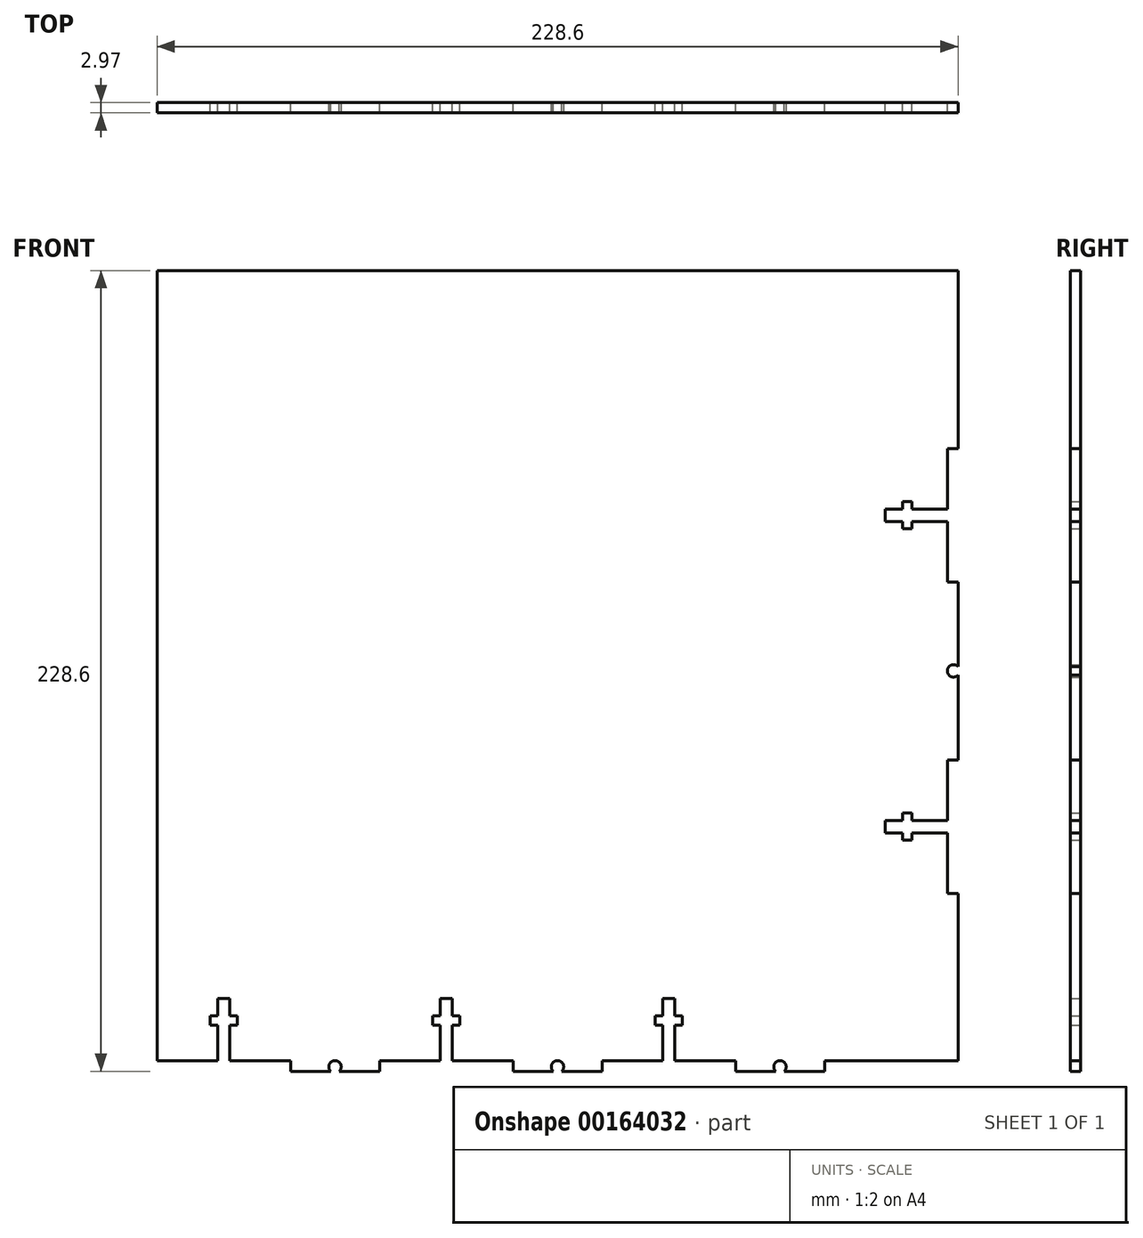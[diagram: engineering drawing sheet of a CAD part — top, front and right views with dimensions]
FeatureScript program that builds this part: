
annotation { "Feature Type Name" : "Feature", "Feature Type Description" : "" }
export const myFeature = defineFeature(function(context is Context, id is Id, definition is map)
    precondition{}
    {
        {
            var Q0;
            Q0=qCreatedBy(makeId("Front.planeOp"),FACE);
            var sketch = newSketch(context, id + "F0", { "sketchPlane" : qUnion([Q0])});
            skLineSegment(sketch, "E0.bottom", {"start": v(114.3, -114.3) * mm, "end": v(-114.3, -114.3) * mm});
            skLineSegment(sketch, "E0.top", {"start": v(114.3, 114.3) * mm, "end": v(-114.3, 114.3) * mm});
            skLineSegment(sketch, "E0.left", {"start": v(114.3, -114.3) * mm, "end": v(114.3, 114.3) * mm});
            skLineSegment(sketch, "E0.right", {"start": v(-114.3, -114.3) * mm, "end": v(-114.3, 114.3) * mm});
            skPoint(sketch, "E0.middle", {"position": v(0, 0) * mm});
            skLineSegment(sketch, "E1.bottom", {"start": v(-114.3, -111.33) * mm, "end": v(-97.02, -111.33) * mm});
            skLineSegment(sketch, "E1.top", {"start": v(-114.3, -114.3) * mm, "end": v(-76.2, -114.3) * mm});
            skLineSegment(sketch, "E1.left", {"start": v(-114.3, -111.33) * mm, "end": v(-114.3, -114.3) * mm});
            skLineSegment(sketch, "E1.right", {"start": v(-76.2, -111.33) * mm, "end": v(-76.2, -114.3) * mm});
            skPoint(sketch, "E2", {"position": v(-95.25, -114.3) * mm});
            skLineSegment(sketch, "E3.bottom", {"start": v(-97.02, -114.3) * mm, "end": v(-93.48, -114.3) * mm});
            skLineSegment(sketch, "E3.top", {"start": v(-97.02, -93.5) * mm, "end": v(-93.48, -93.5) * mm});
            skLineSegment(sketch, "E3.left", {"start": v(-97.02, -111.33) * mm, "end": v(-97.02, -101.17) * mm});
            skLineSegment(sketch, "E3.right", {"start": v(-93.48, -111.33) * mm, "end": v(-93.48, -101.17) * mm});
            skLineSegment(sketch, "E4", {"start": v(-95.25, -114.3) * mm, "end": v(-95.25, -114.3) * mm});
            skPoint(sketch, "E4.endSnap0", {"position": v(-95.25, -93.5) * mm});
            skLineSegment(sketch, "E5.bottom", {"start": v(-91.36, -101.17) * mm, "end": v(-93.48, -101.17) * mm});
            skLineSegment(sketch, "E5.top", {"start": v(-91.36, -98.53) * mm, "end": v(-93.48, -98.53) * mm});
            skLineSegment(sketch, "E5.left", {"start": v(-91.36, -101.17) * mm, "end": v(-91.36, -98.53) * mm});
            skLineSegment(sketch, "E5.right", {"start": v(-99.14, -101.17) * mm, "end": v(-99.14, -98.53) * mm});
            skPoint(sketch, "E5.middle", {"position": v(-95.25, -99.85) * mm});
            skLineSegment(sketch, "E6", {"start": v(-95.25, -114.3) * mm, "end": v(-95.25, -87.14) * mm, "construction": true});
            skLineSegment(sketch, "E7.trimOffspring", {"start": v(-93.48, -98.53) * mm, "end": v(-93.48, -93.5) * mm});
            skLineSegment(sketch, "E8.trimOffspring", {"start": v(-97.02, -98.53) * mm, "end": v(-99.14, -98.53) * mm});
            skLineSegment(sketch, "E9.trimOffspring", {"start": v(-97.02, -98.53) * mm, "end": v(-97.02, -93.5) * mm});
            skLineSegment(sketch, "E10.trimOffspring", {"start": v(-97.02, -101.17) * mm, "end": v(-99.14, -101.17) * mm});
            skLineSegment(sketch, "E11.trimOffspring", {"start": v(-93.48, -111.33) * mm, "end": v(-76.2, -111.33) * mm});
            skLineSegment(sketch, "E12.1.0.0", {"start": v(-50.8, -111.33) * mm, "end": v(-50.8, -114.3) * mm});
            skLineSegment(sketch, "E12.1.0.1", {"start": v(-50.8, -114.3) * mm, "end": v(-12.7, -114.3) * mm});
            skLineSegment(sketch, "E12.1.0.2", {"start": v(-12.7, -111.33) * mm, "end": v(-12.7, -114.3) * mm});
            skLineSegment(sketch, "E12.1.0.3", {"start": v(-29.98, -111.33) * mm, "end": v(-12.7, -111.33) * mm});
            skLineSegment(sketch, "E12.1.0.4", {"start": v(-29.98, -111.33) * mm, "end": v(-29.98, -101.17) * mm});
            skLineSegment(sketch, "E12.1.0.5", {"start": v(-27.86, -101.17) * mm, "end": v(-29.98, -101.17) * mm});
            skLineSegment(sketch, "E12.1.0.6", {"start": v(-27.86, -101.17) * mm, "end": v(-27.86, -98.53) * mm});
            skLineSegment(sketch, "E12.1.0.7", {"start": v(-27.86, -98.53) * mm, "end": v(-29.98, -98.53) * mm});
            skLineSegment(sketch, "E12.1.0.8", {"start": v(-29.98, -98.53) * mm, "end": v(-29.98, -93.5) * mm});
            skLineSegment(sketch, "E12.1.0.9", {"start": v(-33.52, -93.5) * mm, "end": v(-29.98, -93.5) * mm});
            skLineSegment(sketch, "E12.1.0.10", {"start": v(-33.52, -98.53) * mm, "end": v(-33.52, -93.5) * mm});
            skLineSegment(sketch, "E12.1.0.11", {"start": v(-33.52, -98.53) * mm, "end": v(-35.64, -98.53) * mm});
            skLineSegment(sketch, "E12.1.0.12", {"start": v(-35.64, -101.17) * mm, "end": v(-35.64, -98.53) * mm});
            skLineSegment(sketch, "E12.1.0.13", {"start": v(-33.52, -101.17) * mm, "end": v(-35.64, -101.17) * mm});
            skLineSegment(sketch, "E12.1.0.14", {"start": v(-33.52, -111.33) * mm, "end": v(-33.52, -101.17) * mm});
            skLineSegment(sketch, "E12.1.0.15", {"start": v(-50.8, -111.33) * mm, "end": v(-33.52, -111.33) * mm});
            skLineSegment(sketch, "E12.2.0.0", {"start": v(12.7, -111.33) * mm, "end": v(12.7, -114.3) * mm});
            skLineSegment(sketch, "E12.2.0.1", {"start": v(12.7, -114.3) * mm, "end": v(50.8, -114.3) * mm});
            skLineSegment(sketch, "E12.2.0.2", {"start": v(50.8, -111.33) * mm, "end": v(50.8, -114.3) * mm});
            skLineSegment(sketch, "E12.2.0.3", {"start": v(33.52, -111.33) * mm, "end": v(50.8, -111.33) * mm});
            skLineSegment(sketch, "E12.2.0.4", {"start": v(33.52, -111.33) * mm, "end": v(33.52, -101.17) * mm});
            skLineSegment(sketch, "E12.2.0.5", {"start": v(35.64, -101.17) * mm, "end": v(33.52, -101.17) * mm});
            skLineSegment(sketch, "E12.2.0.6", {"start": v(35.64, -101.17) * mm, "end": v(35.64, -98.53) * mm});
            skLineSegment(sketch, "E12.2.0.7", {"start": v(35.64, -98.53) * mm, "end": v(33.52, -98.53) * mm});
            skLineSegment(sketch, "E12.2.0.8", {"start": v(33.52, -98.53) * mm, "end": v(33.52, -93.5) * mm});
            skLineSegment(sketch, "E12.2.0.9", {"start": v(29.98, -93.5) * mm, "end": v(33.52, -93.5) * mm});
            skLineSegment(sketch, "E12.2.0.10", {"start": v(29.98, -98.53) * mm, "end": v(29.98, -93.5) * mm});
            skLineSegment(sketch, "E12.2.0.11", {"start": v(29.98, -98.53) * mm, "end": v(27.86, -98.53) * mm});
            skLineSegment(sketch, "E12.2.0.12", {"start": v(27.86, -101.17) * mm, "end": v(27.86, -98.53) * mm});
            skLineSegment(sketch, "E12.2.0.13", {"start": v(29.98, -101.17) * mm, "end": v(27.86, -101.17) * mm});
            skLineSegment(sketch, "E12.2.0.14", {"start": v(29.98, -111.33) * mm, "end": v(29.98, -101.17) * mm});
            skLineSegment(sketch, "E12.2.0.15", {"start": v(12.7, -111.33) * mm, "end": v(29.98, -111.33) * mm});
            skLineSegment(sketch, "E12.direction1", {"start": v(-114.3, -114.3) * mm, "end": v(-50.8, -114.3) * mm, "construction": true});
            skArc(sketch, "E13", {"start": v(-62.26, -114.3) * mm, "mid": v(-63.5, -111.25) * mm, "end": v(-64.74, -114.3) * mm});
            skArc(sketch, "E14.1.0.0", {"start": v(1.24, -114.3) * mm, "mid": v(0, -111.25) * mm, "end": v(-1.24, -114.3) * mm});
            skArc(sketch, "E14.2.0.0", {"start": v(64.74, -114.3) * mm, "mid": v(63.5, -111.25) * mm, "end": v(62.26, -114.3) * mm});
            skLineSegment(sketch, "E14.direction1", {"start": v(-63.5, -113.03) * mm, "end": v(0, -113.03) * mm, "construction": true});
            skLineSegment(sketch, "E15.bottom", {"start": v(114.3, -111.33) * mm, "end": v(76.2, -111.33) * mm});
            skLineSegment(sketch, "E15.top", {"start": v(114.3, -114.3) * mm, "end": v(76.2, -114.3) * mm});
            skLineSegment(sketch, "E15.left", {"start": v(114.3, -111.33) * mm, "end": v(114.3, -114.3) * mm});
            skLineSegment(sketch, "E15.right", {"start": v(76.2, -111.33) * mm, "end": v(76.2, -114.3) * mm});
            skLineSegment(sketch, "E16.bottom", {"start": v(114.3, -63.5) * mm, "end": v(111.33, -63.5) * mm});
            skLineSegment(sketch, "E16.top", {"start": v(114.3, -25.4) * mm, "end": v(111.33, -25.4) * mm});
            skLineSegment(sketch, "E16.left", {"start": v(114.3, -63.5) * mm, "end": v(114.3, -25.4) * mm});
            skLineSegment(sketch, "E16.right", {"start": v(111.33, -63.5) * mm, "end": v(111.33, -46.22) * mm});
            skLineSegment(sketch, "E17.bottom", {"start": v(93.5, -42.68) * mm, "end": v(98.53, -42.68) * mm});
            skLineSegment(sketch, "E17.top", {"start": v(93.5, -46.22) * mm, "end": v(98.53, -46.22) * mm});
            skLineSegment(sketch, "E17.left", {"start": v(93.5, -42.68) * mm, "end": v(93.5, -46.22) * mm});
            skLineSegment(sketch, "E17.right", {"start": v(114.3, -42.68) * mm, "end": v(114.3, -46.22) * mm});
            skPoint(sketch, "E18", {"position": v(114.3, -44.45) * mm});
            skLineSegment(sketch, "E19", {"start": v(114.3, -44.45) * mm, "end": v(83.34, -44.45) * mm, "construction": true});
            skLineSegment(sketch, "E20.bottom", {"start": v(101.17, -48.34) * mm, "end": v(98.53, -48.34) * mm});
            skLineSegment(sketch, "E20.top", {"start": v(101.17, -40.56) * mm, "end": v(98.53, -40.56) * mm});
            skLineSegment(sketch, "E20.left", {"start": v(101.17, -48.34) * mm, "end": v(101.17, -46.22) * mm});
            skLineSegment(sketch, "E20.right", {"start": v(98.53, -48.34) * mm, "end": v(98.53, -46.22) * mm});
            skPoint(sketch, "E20.middle", {"position": v(99.85, -44.45) * mm});
            skLineSegment(sketch, "E21.trimOffspring", {"start": v(111.33, -42.68) * mm, "end": v(111.33, -25.4) * mm});
            skLineSegment(sketch, "E22.trimOffspring", {"start": v(101.17, -42.68) * mm, "end": v(111.33, -42.68) * mm});
            skLineSegment(sketch, "E23.trimOffspring", {"start": v(101.17, -42.68) * mm, "end": v(101.17, -40.56) * mm});
            skLineSegment(sketch, "E24.trimOffspring", {"start": v(101.17, -46.22) * mm, "end": v(111.33, -46.22) * mm});
            skLineSegment(sketch, "E25.trimOffspring", {"start": v(98.53, -42.68) * mm, "end": v(98.53, -40.56) * mm});
            skPoint(sketch, "E26.0.1.0", {"position": v(99.85, 44.45) * mm});
            skLineSegment(sketch, "E26.0.1.1", {"start": v(101.17, 46.22) * mm, "end": v(111.33, 46.22) * mm});
            skLineSegment(sketch, "E26.0.1.2", {"start": v(111.33, 46.22) * mm, "end": v(111.33, 63.5) * mm});
            skLineSegment(sketch, "E26.0.1.3", {"start": v(111.33, 25.4) * mm, "end": v(111.33, 42.68) * mm});
            skLineSegment(sketch, "E26.0.1.4", {"start": v(114.3, 25.4) * mm, "end": v(114.3, 63.5) * mm});
            skLineSegment(sketch, "E26.0.1.5", {"start": v(114.3, 63.5) * mm, "end": v(111.33, 63.5) * mm});
            skLineSegment(sketch, "E26.0.1.6", {"start": v(114.3, 46.22) * mm, "end": v(114.3, 42.68) * mm});
            skLineSegment(sketch, "E26.0.1.7", {"start": v(114.3, 25.4) * mm, "end": v(111.33, 25.4) * mm});
            skLineSegment(sketch, "E26.0.1.8", {"start": v(101.17, 42.68) * mm, "end": v(111.33, 42.68) * mm});
            skLineSegment(sketch, "E26.0.1.9", {"start": v(93.5, 42.68) * mm, "end": v(98.53, 42.68) * mm});
            skLineSegment(sketch, "E26.0.1.10", {"start": v(101.17, 46.22) * mm, "end": v(101.17, 48.34) * mm});
            skLineSegment(sketch, "E26.0.1.11", {"start": v(101.17, 48.34) * mm, "end": v(98.53, 48.34) * mm});
            skLineSegment(sketch, "E26.0.1.12", {"start": v(101.17, 40.56) * mm, "end": v(98.53, 40.56) * mm});
            skLineSegment(sketch, "E26.0.1.13", {"start": v(98.53, 46.22) * mm, "end": v(98.53, 48.34) * mm});
            skLineSegment(sketch, "E26.0.1.14", {"start": v(101.17, 40.56) * mm, "end": v(101.17, 42.68) * mm});
            skLineSegment(sketch, "E26.0.1.15", {"start": v(98.53, 40.56) * mm, "end": v(98.53, 42.68) * mm});
            skLineSegment(sketch, "E26.0.1.16", {"start": v(93.5, 46.22) * mm, "end": v(93.5, 42.68) * mm});
            skLineSegment(sketch, "E26.0.1.17", {"start": v(93.5, 46.22) * mm, "end": v(98.53, 46.22) * mm});
            skLineSegment(sketch, "E26.direction1", {"start": v(93.5, -46.22) * mm, "end": v(118.9, -46.22) * mm, "construction": true});
            skLineSegment(sketch, "E26.direction2", {"start": v(93.5, -46.22) * mm, "end": v(93.5, 42.68) * mm, "construction": true});
            skArc(sketch, "E27", {"start": v(114.3, 1.24) * mm, "mid": v(111.25, 0) * mm, "end": v(114.3, -1.24) * mm});
            skSolve(sketch);
        }
        {
            var Q0;
            Q0=makeQuery(id+"F0.imprint","IMPRINT",FACE,{"disambiguationData":[TD([[makeQuery(id+"F0.imprint","IMPRINT",EDGE,{"derivedFrom":sQuery(id+"F0.wireOp",EDGE,"E0.top")}),1.0]])]});
            extrude(context, id + "F1", {"entities" : qUnion([Q0]), "depth" : 2.97 * mm});
        }
    });
